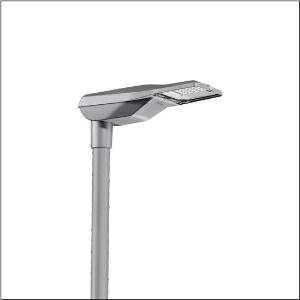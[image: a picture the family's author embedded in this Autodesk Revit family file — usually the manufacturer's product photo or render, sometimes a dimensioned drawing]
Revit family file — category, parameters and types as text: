
# Revit family: streetlight_sl_21_iq_micro___st1_5a_5xe1p41g08cb_60b9
name_source: partatom
category: Lighting Fixtures
units: mm (PartAtom-declared; Revit-internal decimal feet)

## family parameters
Cut with Voids When Loaded = No
Host = Face
Light Source = No
Part Type = Normal
Room Calculation Point = No
Round Connector Dimension = Use Diameter
Shared = No

## types (1)
- --- (1 x LED, 2930 lm, 19.4 W, 4000K)
    Apparent Load = 19 VA
    CIE Flux Codes = 22 53 95 100 100
    Color Rendering = 70
    Color Temperature = 4000K
    Default Elevation = 1800 mm
    Description = Streetlight SL 21 iQ micro, mast luminaire, primary light control with lens, of PMMA, primary optical cover: cover, of toughened safety glass, transparent, light distribution: ST1.5a, light emission: direct distribution, primary light characteristic: asymmetric, installation type: post-top, side-entry, LED, High Power LED, rated luminous flux: 2.930lm, luminous efficacy: 151lm/W, light colour: 740, colour temperature: 4000K, control: Street-Remote, Auto-Match, Temp-Guard, Lumen-Switch, Night-Set, Smart-Wire, Light-Fading, Desk-Remote (wireless, voltage-free reading and setting of iQ features in the workshop via application-optimized NFC function/RFID function), optimised constant luminous flux control (CLO 2.0), pre-setting: linear dimming characteristic, mains connection: 220..240V, AC, 50/60Hz, start of lifetime: 19W, end of service life: 20W, reduction: 10W, luminaire housing, of diecast aluminium, powder-coated, Siteco® metallic grey (DB 702S), corrosivity category C5 mid according to DIN EN ISO 12944, please order mast flange separately, inclination adjustable: 0°, 5°, 10°, 15°, sealing non-destructively replaceable, multi-level sealing system, length: 528mm, width: 235mm, height: 110mm, mast flange for spigot size: 42mm (side-entry): 5XC10008XM4, 60/48mm (side-entry/post-top): 5XC10108XM2, 76/60mm (side-entry/post-top): 5XC10108XM1, protection rating (complete): IP66, insulation class (complete): insulation class II (safety insulation), certification: CE, ENEC, ENEC+, VDE, impact resistance: IK09, permissible operating ambient temperature for outdoor applications: -40..+50°C, standard-compliant lighting for roads and squares, packaging unit: 1 piece

Light Distribution: ST1.5a
    Height = 110 mm
    Lamp = 1 x LED
    Lamp Light Flux = 2930 lm
    Lamp Power = 19.4 W
    Lamp count = 1
    Length = 528 mm
    Luminous efficacy = 151 lm/W
    Manufacturer = Siteco
    ModVariant = No
    Model = 5XE1P41G08CB
    Number of Poles = 1
    OnlyDefault = Yes
    Power Factor = 1
    Product Name = Streetlight SL 21 iQ micro | ST1.5a
    Product group = mast luminaire | pylon top
    ProductGroupID = 6100
    Protection Class = Protection class II
    Protection Degree = IP 66
    RLX_Detail_Level = 1
    RLX_Emergency_Light_Flux = 0 lm
    RLX_Emergency_Type = 0
    RLX_Emergency_Type_DB = No
    RlxData = <blob elided: 103709 chars, md5=9d4ff032>
    Socket = socket
    Standby Power = 0 W
    System Light Flux = 2930 lm
    System Power = 19 W
    Type Comments = factory setting: luminous flux: 100 % | dim-lin: 254 | 387 mA
    Type Image = l_1006881.jpg
    URL = http://relux.com
    VarID = @adj_107803
    Voltage = 0 V
    Weight = 0.00 kg
    Width = 235 mm

## geometry (parser evidence)
native form markers: Blend x4, Sweep x10
no freeform markers — native parametric forms only
